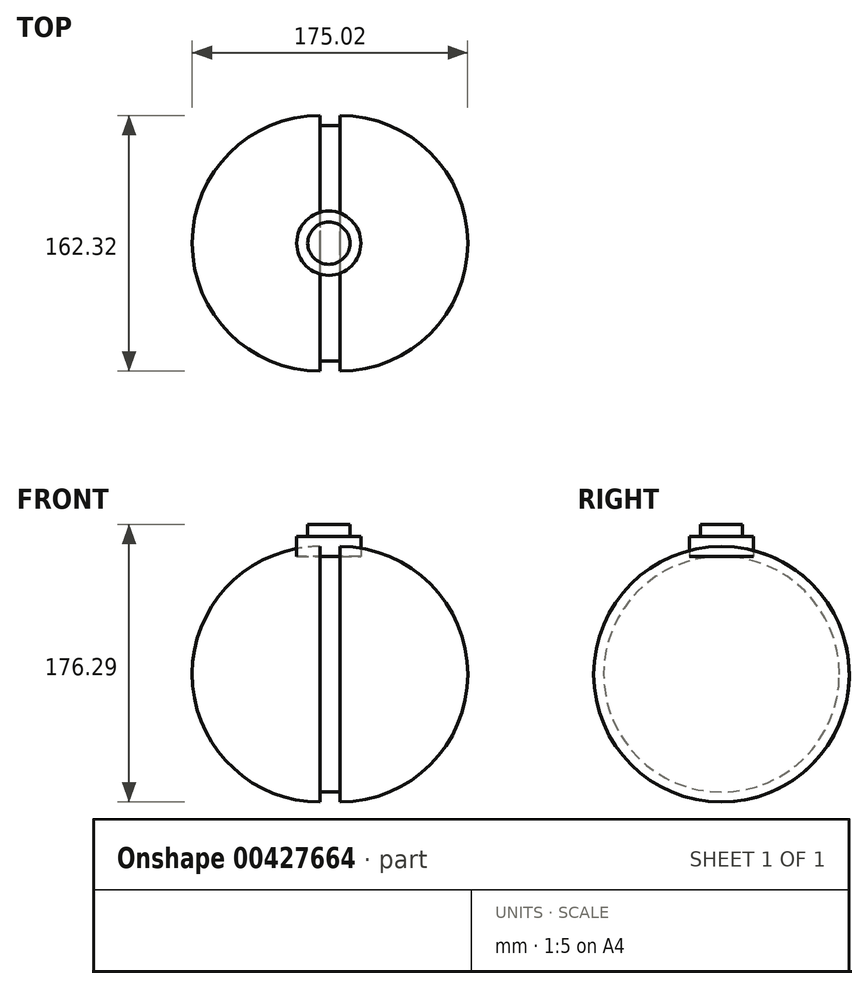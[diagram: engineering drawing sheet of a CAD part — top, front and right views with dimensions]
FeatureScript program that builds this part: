
annotation { "Feature Type Name" : "Feature", "Feature Type Description" : "" }
export const myFeature = defineFeature(function(context is Context, id is Id, definition is map)
    precondition{}
    {
        {
            var Q0;
            Q0=qCreatedBy(makeId("Right.planeOp"),FACE);
            var sketch = newSketch(context, id + "F0", { "sketchPlane" : qUnion([Q0])});
            skCircle(sketch, "E0", {"center": v(0, 0) * mm, "radius": 74.81 * mm});
            skSolve(sketch);
        }
        {
            var Q0;
            Q0=makeQuery(id+"F0.imprint","IMPRINT",FACE,{"disambiguationData":[TD([[makeQuery(id+"F0.imprint","IMPRINT",EDGE,{"derivedFrom":sQuery(id+"F0.wireOp",EDGE,"E0")}),1.0]])]});
            extrude(context, id + "F1", {"entities" : qUnion([Q0]), "depth" : 12.7 * mm});
        }
        {
            var Q0;
            Q0=makeQuery(id+"F1.opExtrude","CAP_FACE",FACE,{"disambiguationData":[OSD([sQuery(id+"F0.wireOp",EDGE,"E0")])],"isStart":true});
            var sketch = newSketch(context, id + "F2", { "sketchPlane" : qUnion([Q0])});
            skPoint(sketch, "E1", {"position": v(0, 74.81) * mm});
            skSolve(sketch);
        }
        {
            var Q0;
            Q0=qCreatedBy(makeId("Top.planeOp"),FACE);
            var Q1;
            Q1=sQuery(id+"F2.wireOp",VERTEX,"E1");
            cPlane(context, id + "F3", {"entities" : qUnion([Q0, Q1]), "cplaneType" : CPlaneType.PLANE_POINT, "offset" : 25.4 * mm, "width" : 152.4 * mm, "height" : 152.4 * mm});
        }
        {
            var Q0;
            Q0=qCreatedBy(id+"F3.planeOp",FACE);
            var sketch = newSketch(context, id + "F4", { "sketchPlane" : qUnion([Q0])});
            skCircle(sketch, "E2", {"center": v(5.65, 0) * mm, "radius": 20.37 * mm});
            skSolve(sketch);
        }
        {
            var Q0;
            Q0=makeQuery(id+"F4.imprint","IMPRINT",FACE,{"disambiguationData":[TD([[makeQuery(id+"F4.imprint","IMPRINT",EDGE,{"derivedFrom":sQuery(id+"F4.wireOp",EDGE,"E2")}),1.0]])]});
            extrude(context, id + "F5", {"entities" : qUnion([Q0]), "operationType" : NewBodyOperationType.ADD, "depth" : 12.7 * mm});
        }
        {
            var Q0;
            Q0=makeQuery(id+"F5.opExtrude","CAP_FACE",FACE,{"disambiguationData":[OSD([sQuery(id+"F4.wireOp",EDGE,"E2")])],"isStart":false});
            var sketch = newSketch(context, id + "F6", { "sketchPlane" : qUnion([Q0])});
            skCircle(sketch, "E3", {"center": v(5.65, 0) * mm, "radius": 13.4 * mm});
            skSolve(sketch);
        }
        {
            var Q0;
            Q0=makeQuery(id+"F6.imprint","IMPRINT",FACE,{"disambiguationData":[TD([[makeQuery(id+"F6.imprint","IMPRINT",EDGE,{"derivedFrom":sQuery(id+"F6.wireOp",EDGE,"E3")}),1.0]])]});
            extrude(context, id + "F7", {"entities" : qUnion([Q0]), "operationType" : NewBodyOperationType.ADD, "depth" : 7.62 * mm});
        }
        {
            var Q0;
            Q0=makeQuery(id+"F2.imprint","IMPRINT",FACE,{"disambiguationData":[TD([[makeQuery(id+"F2.imprint","IMPRINT",EDGE,{"derivedFrom":makeQuery(id+"F1.opExtrude","CAP_EDGE",EDGE,{"disambiguationData":[OSD([sQuery(id+"F0.wireOp",EDGE,"E0")])],"isStart":true})}),-1.0]])]});
            var sketch = newSketch(context, id + "F8", { "sketchPlane" : qUnion([Q0])});
            skSolve(sketch);
        }
        {
            var Q0;
            Q0=makeQuery(id+"F1.opExtrude","CAP_FACE",FACE,{"disambiguationData":[OSD([sQuery(id+"F0.wireOp",EDGE,"E0")])],"isStart":false});
            var sketch = newSketch(context, id + "F9", { "sketchPlane" : qUnion([Q0])});
            skLineSegment(sketch, "E4", {"start": v(0, 81.16) * mm, "end": v(0, -81.16) * mm});
            skArc(sketch, "E5.0", {"start": v(0, -81.16) * mm, "mid": v(81.16, 0) * mm, "end": v(0, 81.16) * mm});
            skPoint(sketch, "E6.orphan", {"position": v(0, 74.81) * mm});
            skSolve(sketch);
        }
        {
            var Q0;
            Q0 = qSketchRegion(id + "F9", true);
            var Q1;
            Q1=sQuery(id+"F9.wireOp",EDGE,"E4");
            revolve(context, id + "F10", {"entities" : qUnion([Q0]), "axis" : qUnion([Q1]), "revolveType" : RevolveType.ONE_DIRECTION, "angle" : 180 * degree});
        }
        {
            var Q0;
            Q0=makeQuery(id+"F8.imprint","IMPRINT",FACE,{"disambiguationData":[TD([[makeQuery(id+"F8.imprint","IMPRINT",EDGE,{"derivedFrom":makeQuery(id+"F2.imprint","IMPRINT",EDGE,{"derivedFrom":makeQuery(id+"F1.opExtrude","CAP_EDGE",EDGE,{"disambiguationData":[OSD([sQuery(id+"F0.wireOp",EDGE,"E0")])],"isStart":true})})}),-1.0]])]});
            var sketch = newSketch(context, id + "F11", { "sketchPlane" : qUnion([Q0])});
            skPoint(sketch, "E7.orphan", {"position": v(0, 74.81) * mm});
            skArc(sketch, "E8.0", {"start": v(0, -81.16) * mm, "mid": v(81.16, 0) * mm, "end": v(0, 81.16) * mm});
            skLineSegment(sketch, "E9", {"start": v(0, 81.16) * mm, "end": v(0, -81.16) * mm});
            skPoint(sketch, "E10.orphan", {"position": v(0, 38.74) * mm});
            skSolve(sketch);
        }
        {
            var Q0;
            Q0 = qSketchRegion(id + "F11", true);
            var Q1;
            Q1=sQuery(id+"F11.wireOp",EDGE,"E9");
            revolve(context, id + "F12", {"entities" : qUnion([Q0]), "axis" : qUnion([Q1]), "revolveType" : RevolveType.ONE_DIRECTION, "angle" : 180 * degree});
        }
    });
